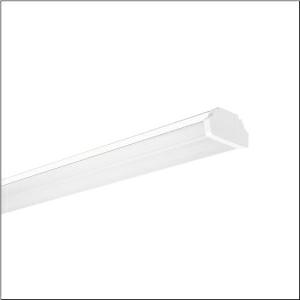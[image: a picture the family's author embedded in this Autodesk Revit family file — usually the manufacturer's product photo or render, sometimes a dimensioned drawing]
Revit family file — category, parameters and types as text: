
# Revit family: modario_31_gen_2_53bm8127v68xc2_a15f
name_source: partatom
category: Lighting Fixtures
units: mm (PartAtom-declared; Revit-internal decimal feet)

## family parameters
Cut with Voids When Loaded = No
Host = Face
Light Source = No
Part Type = Normal
Room Calculation Point = No
Round Connector Dimension = Use Diameter
Shared = No

## types (1)
- Modario 31 Gen.2 (1 x LED, 8340 lm, 47.9 W, 6500K)
    Apparent Load = 48 VA
    CIE Flux Codes = 47 80 95 93 100
    Color Rendering = 80
    Color Temperature = 6500K
    Default Elevation = 1800 mm
    Description = Modario 31 Gen.2, luminaire insert, of sheet steel, coil coated, white, length: 1.495mm, width: 81mm, height: 82mm, 5x system unit, system units: 299mm, LED rated luminous flux: 8.340lm, light colour: 865, SDCM (Standard Deviation of Colour Matching)MacAdam ≤ 3 SDCM (initial), control gear: ON/OFF, control gear: ECG, with plug, 3-pole, with phase selection, mains connection: 220..240V, AC, 50/60Hz, rated input power: 48W, through-wiring accessed according to module size, primary optical cover: cover, of PMMA, light emission: direct distribution, primary light characteristic: symmetric, protection rating (complete): IP20, protection rating (LED compartment): IP50, insulation class (complete): insulation class I (protective earthing), certification: CE, ENEC, VDE, UKCA, impact resistance: IK03, permissible ambient temperature for indoor applications: -35..+45°C, corresponds to IFS (International Featured Standards) requirements for safety and quality in the food industry, reducing of maximum allowable ambient temperature of 5°C with ceiling mounting, IP40 when using the optional accessory 5TP9018, packaging unit: 1 piece
    Height = 92 mm
    Lamp = 1 x LED
    Lamp Light Flux = 8340 lm
    Lamp Power = 47.9 W
    Lamp count = 1
    Length = 1495 mm
    Luminous efficacy = 174 lm/W
    Manufacturer = Siteco
    ModVariant = No
    Model = 53BM8127V68XC2
    Mounting Place = Ceiling
    Mounting Type = Pendant
    Number of Poles = 1
    OnlyDefault = Yes
    Power Factor = 1
    Product Name = Modario 31 Gen.2
    Product group = luminaire insert | ceiling pendant
    ProductGroupID = 901
    Protection Class = Protection class I
    Protection Degree = IP 20
    RLX_Detail_Level = 1
    RLX_Emergency_Light_Flux = 0 lm
    RLX_Emergency_Type = 0
    RLX_Emergency_Type_DB = No
    RlxData = <blob elided: 38497 chars, md5=adbc7e63>
    Socket = socket
    Standby Power = 0 W
    System Light Flux = 8340 lm
    System Power = 48 W
    Type Comments = Product without accessories
    Type Image = l_1341886.jpg
    URL = http://relux.com
    VarID = ---
    Voltage = 0 V
    Weight = 0.00 kg
    Width = 81 mm

## geometry (parser evidence)
native form markers: Blend x4, Sweep x11
no freeform markers — native parametric forms only
